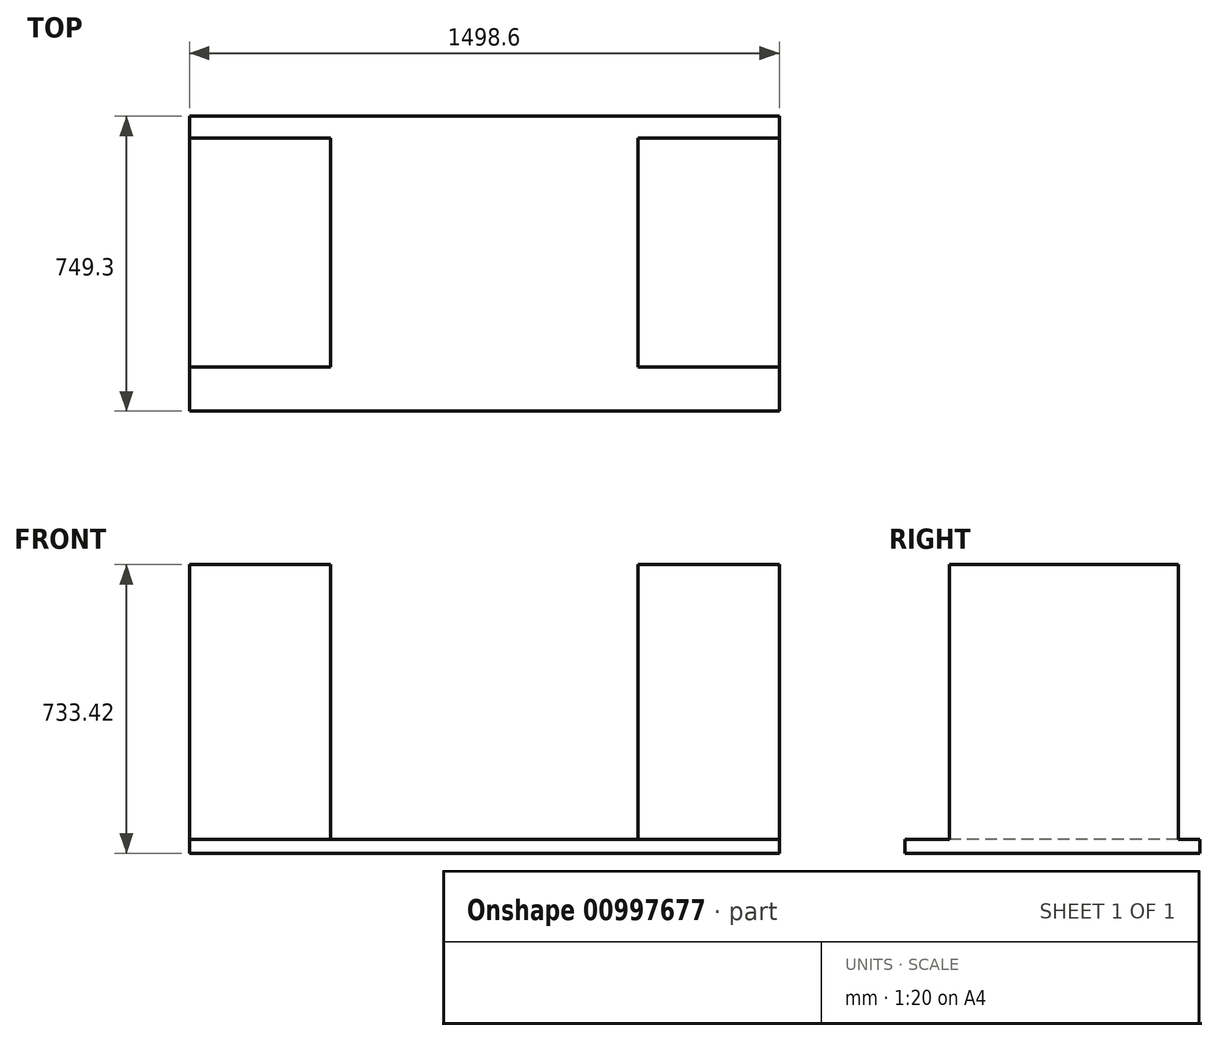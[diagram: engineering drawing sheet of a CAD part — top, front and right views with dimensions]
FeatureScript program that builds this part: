
annotation { "Feature Type Name" : "Feature", "Feature Type Description" : "" }
export const myFeature = defineFeature(function(context is Context, id is Id, definition is map)
    precondition{}
    {
        {
            var Q0;
            Q0=qCreatedBy(makeId("Top.planeOp"),FACE);
            var sketch = newSketch(context, id + "F0", { "sketchPlane" : qUnion([Q0])});
            skLineSegment(sketch, "E0.bottom", {"start": v(749.3, 374.65) * mm, "end": v(-749.3, 374.65) * mm});
            skLineSegment(sketch, "E0.top", {"start": v(749.3, -374.65) * mm, "end": v(-749.3, -374.65) * mm});
            skLineSegment(sketch, "E0.left", {"start": v(749.3, 374.65) * mm, "end": v(749.3, -374.65) * mm});
            skLineSegment(sketch, "E0.right", {"start": v(-749.3, 374.65) * mm, "end": v(-749.3, -374.65) * mm});
            skPoint(sketch, "E0.middle", {"position": v(0, 0) * mm});
            skSolve(sketch);
        }
        {
            var Q0;
            Q0=makeQuery(id+"F0.imprint","IMPRINT",FACE,{"disambiguationData":[TD([[makeQuery(id+"F0.imprint","IMPRINT",EDGE,{"derivedFrom":sQuery(id+"F0.wireOp",EDGE,"E0.bottom")}),1.0]])]});
            extrude(context, id + "F1", {"entities" : qUnion([Q0]), "depth" : 34.92 * mm, "offsetDistance" : 25.4 * mm});
        }
        {
            var Q0;
            Q0=makeQuery(id+"F1.opExtrude","CAP_FACE",FACE,{"disambiguationData":[OSD([sQuery(id+"F0.wireOp",EDGE,"E0.bottom"),sQuery(id+"F0.wireOp",EDGE,"E0.top"),sQuery(id+"F0.wireOp",EDGE,"E0.left"),sQuery(id+"F0.wireOp",EDGE,"E0.right")])],"isStart":false});
            var sketch = newSketch(context, id + "F2", { "sketchPlane" : qUnion([Q0])});
            skLineSegment(sketch, "E1.bottom", {"start": v(-749.3, 318.84) * mm, "end": v(-390.52, 318.84) * mm});
            skLineSegment(sketch, "E1.top", {"start": v(-749.3, -262.19) * mm, "end": v(-390.52, -262.19) * mm});
            skLineSegment(sketch, "E1.left", {"start": v(-749.3, 318.84) * mm, "end": v(-749.3, -262.19) * mm});
            skLineSegment(sketch, "E1.right", {"start": v(-390.52, 318.84) * mm, "end": v(-390.52, -262.19) * mm});
            skLineSegment(sketch, "E2", {"start": v(0, 374.65) * mm, "end": v(0, -374.65) * mm});
            skLineSegment(sketch, "E3.MirrorCS", {"start": v(390.53, 318.84) * mm, "end": v(390.53, -262.19) * mm});
            skLineSegment(sketch, "E4.MirrorCS", {"start": v(749.3, 318.84) * mm, "end": v(390.53, 318.84) * mm});
            skLineSegment(sketch, "E5.MirrorCS", {"start": v(749.3, -262.19) * mm, "end": v(390.53, -262.19) * mm});
            skLineSegment(sketch, "E6.MirrorCS", {"start": v(749.3, 318.84) * mm, "end": v(749.3, -262.19) * mm});
            skSolve(sketch);
        }
        {
            var Q0;
            Q0=makeQuery(id+"F2.imprint","IMPRINT",FACE,{"disambiguationData":[TD([[makeQuery(id+"F2.imprint","IMPRINT",EDGE,{"derivedFrom":sQuery(id+"F2.wireOp",EDGE,"E1.bottom")}),-1.0]])]});
            var Q1;
            Q1=makeQuery(id+"F2.imprint","IMPRINT",FACE,{"disambiguationData":[TD([[makeQuery(id+"F2.imprint","IMPRINT",EDGE,{"derivedFrom":sQuery(id+"F2.wireOp",EDGE,"E3.MirrorCS")}),1.0]])]});
            extrude(context, id + "F3", {"entities" : qUnion([Q0, Q1]), "operationType" : NewBodyOperationType.ADD, "depth" : 698.5 * mm, "offsetDistance" : 25.4 * mm});
        }
    });
